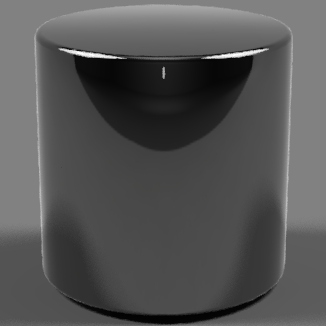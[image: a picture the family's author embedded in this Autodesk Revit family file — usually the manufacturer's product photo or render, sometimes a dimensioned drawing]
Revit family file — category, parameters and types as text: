
# Revit family: BLE-F-WHB-LED
name_source: partatom
category: Lighting Fixtures
units: mm (PartAtom-declared; Revit-internal decimal feet)

## family parameters
Cut with Voids When Loaded = No
Host = Face
Light Source = Yes
Maintain Annotation Orientation = No
Part Type = Normal
Room Calculation Point = No
Round Connector Dimension = Use Diameter
Shared = No

## types (8) — shared parameters
Base Material = 100 - Black
Color Filter = 16777215
Default Elevation = 4' - 0"
Dimming Lamp Color Temperature Shift = <None>
Emit from Line Length = 2' - 0"
Photometric Web File = generic
Shade Material = 100 - Black
Tilt Angle = -90.00°

## per-type parameters (varying)
| type | 11" | 13" | 15" | 17" | Dome | Flat | Heat Sink | Heat Sink 6" | Heat Sink 9" | Light Source |
| 11" Dome | Yes | No | No | No | Yes | No | 0' - 3 3/32" | Yes | No | 0' - 8 3/32" |
| 13" Dome | No | Yes | No | No | Yes | No | 0' - 3 1/2" | No | Yes | 0' - 8 1/2" |
| 15" Dome | No | No | Yes | No | Yes | No | 0' - 3 11/32" | No | Yes | 0' - 8 11/32" |
| 17" Dome | No | No | No | Yes | Yes | No | 0' - 3 11/32" | No | Yes | 0' - 8 11/32" |
| 11" Flat | Yes | No | No | No | No | Yes | 0' - 3 3/32" | Yes | No | 0' - 8 3/32" |
| 13" Flat | No | Yes | No | No | No | Yes | 0' - 3 1/2" | No | Yes | 0' - 8 1/2" |
| 15" Flat | No | No | Yes | No | No | Yes | 0' - 3 11/32" | Yes | Yes | 0' - 8 11/32" |
| 17" Flat | No | No | No | Yes | No | Yes | 0' - 3 11/32" | No | Yes | 0' - 8 11/32" |

## geometry (parser evidence)
native form markers: Sweep x38
no freeform markers — native parametric forms only
